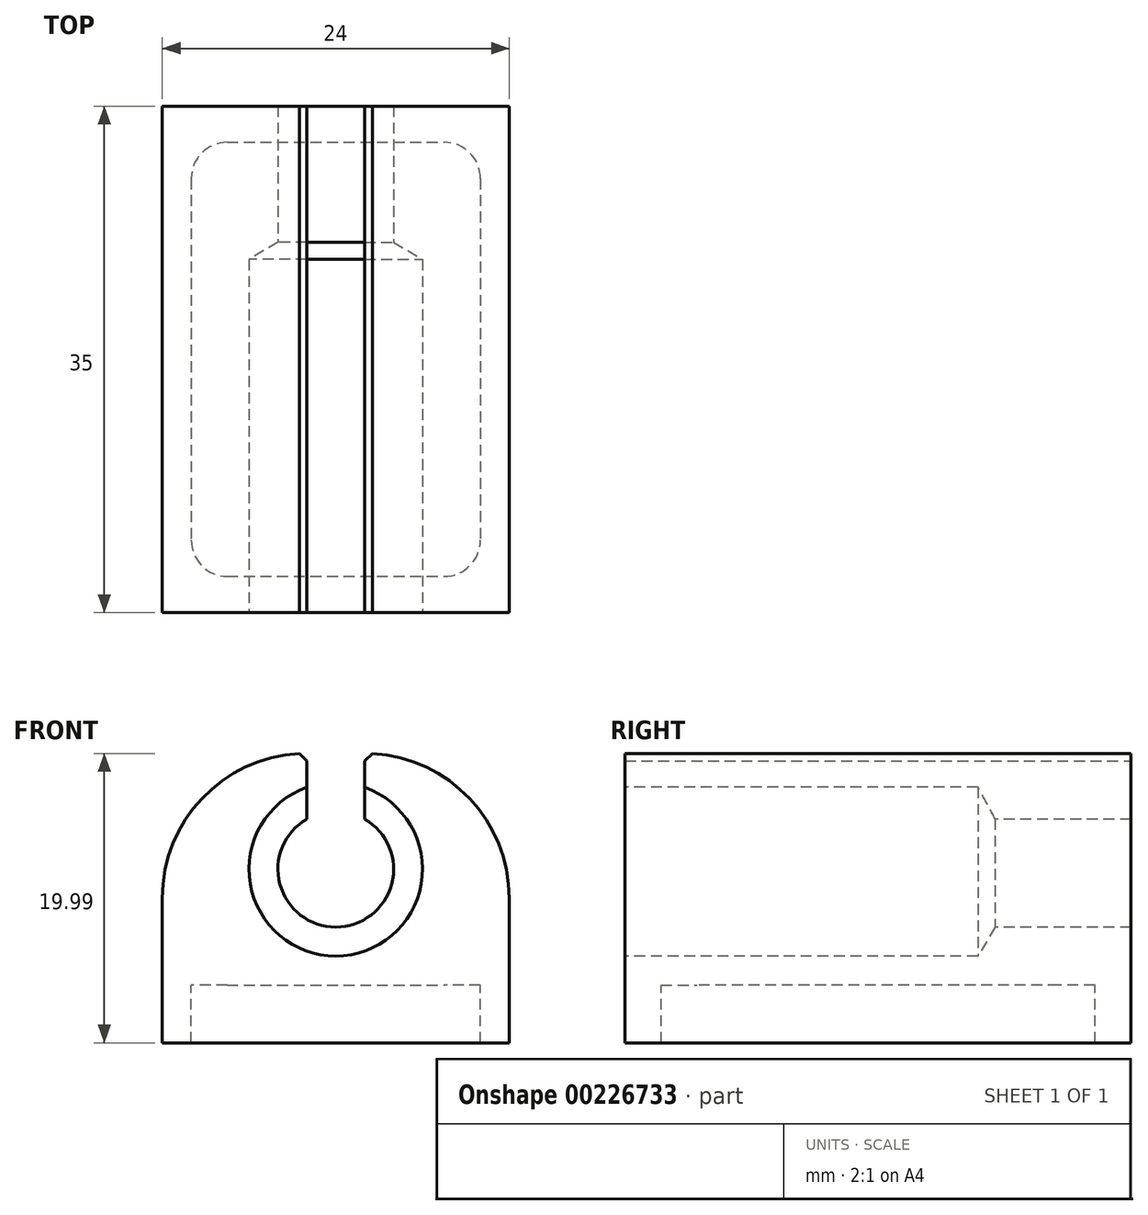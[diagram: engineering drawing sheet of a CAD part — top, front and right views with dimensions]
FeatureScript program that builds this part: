
annotation { "Feature Type Name" : "Feature", "Feature Type Description" : "" }
export const myFeature = defineFeature(function(context is Context, id is Id, definition is map)
    precondition{}
    {
        {
            var Q0;
            Q0=qCreatedBy(makeId("Top.planeOp"),FACE);
            var sketch = newSketch(context, id + "F0", { "sketchPlane" : qUnion([Q0])});
            skLineSegment(sketch, "E0.bottom", {"start": v(0, 12.5) * mm, "end": v(10, 12.5) * mm});
            skLineSegment(sketch, "E0.top", {"start": v(0, -12.5) * mm, "end": v(10, -12.5) * mm});
            skLineSegment(sketch, "E0.left", {"start": v(0, 12.5) * mm, "end": v(0, -12.5) * mm});
            skLineSegment(sketch, "E0.right", {"start": v(10, 12.5) * mm, "end": v(10, -12.5) * mm});
            skLineSegment(sketch, "E1.bottom", {"start": v(0, 12.5) * mm, "end": v(-10, 12.5) * mm});
            skLineSegment(sketch, "E1.top", {"start": v(0, -12.5) * mm, "end": v(-10, -12.5) * mm});
            skLineSegment(sketch, "E1.right", {"start": v(-10, 12.5) * mm, "end": v(-10, -12.5) * mm});
            skLineSegment(sketch, "E2.bottom", {"start": v(-12, 17.5) * mm, "end": v(12, 17.5) * mm});
            skLineSegment(sketch, "E2.top", {"start": v(-12, -17.5) * mm, "end": v(12, -17.5) * mm});
            skLineSegment(sketch, "E2.left", {"start": v(-12, 17.5) * mm, "end": v(-12, -17.5) * mm});
            skLineSegment(sketch, "E2.right", {"start": v(12, 17.5) * mm, "end": v(12, -17.5) * mm});
            skArc(sketch, "E3", {"start": v(-10, 12.5) * mm, "mid": v(-9.27, 14.27) * mm, "end": v(-7.5, 15) * mm});
            skLineSegment(sketch, "E4", {"start": v(-7.5, 15) * mm, "end": v(7.5, 15) * mm});
            skArc(sketch, "E5", {"start": v(10, 12.5) * mm, "mid": v(9.27, 14.27) * mm, "end": v(7.5, 15) * mm});
            skArc(sketch, "E6", {"start": v(10, -12.5) * mm, "mid": v(9.27, -14.27) * mm, "end": v(7.5, -15) * mm});
            skArc(sketch, "E7", {"start": v(-10, -12.5) * mm, "mid": v(-9.27, -14.27) * mm, "end": v(-7.5, -15) * mm});
            skLineSegment(sketch, "E8", {"start": v(-7.5, -15) * mm, "end": v(7.5, -15) * mm});
            skSolve(sketch);
        }
        {
            var Q0;
            Q0=makeQuery(id+"F0.imprint","IMPRINT",FACE,{"disambiguationData":[TD([[makeQuery(id+"F0.imprint","IMPRINT",EDGE,{"derivedFrom":sQuery(id+"F0.wireOp",EDGE,"E0.right")}),1.0]])]});
            extrude(context, id + "F1", {"entities" : qUnion([Q0]), "oppositeDirection" : true, "depth" : 4 * mm});
        }
        {
            var Q0;
            Q0=makeQuery(id+"F0.imprint","IMPRINT",FACE,{"disambiguationData":[TD([[makeQuery(id+"F0.imprint","IMPRINT",EDGE,{"derivedFrom":sQuery(id+"F0.wireOp",EDGE,"E0.bottom")}),-1.0]])]});
            var Q1;
            Q1=makeQuery(id+"F0.imprint","IMPRINT",FACE,{"disambiguationData":[TD([[makeQuery(id+"F0.imprint","IMPRINT",EDGE,{"derivedFrom":sQuery(id+"F0.wireOp",EDGE,"E1.bottom")}),1.0]])]});
            var Q2;
            Q2=makeQuery(id+"F0.imprint","IMPRINT",FACE,{"disambiguationData":[TD([[makeQuery(id+"F0.imprint","IMPRINT",EDGE,{"derivedFrom":sQuery(id+"F0.wireOp",EDGE,"E0.top")}),-1.0]])]});
            var Q3;
            Q3=makeQuery(id+"F0.imprint","IMPRINT",FACE,{"disambiguationData":[TD([[makeQuery(id+"F0.imprint","IMPRINT",EDGE,{"derivedFrom":sQuery(id+"F0.wireOp",EDGE,"E0.bottom")}),1.0]])]});
            var Q4;
            Q4=makeQuery(id+"F0.imprint","IMPRINT",FACE,{"disambiguationData":[TD([[makeQuery(id+"F0.imprint","IMPRINT",EDGE,{"derivedFrom":sQuery(id+"F0.wireOp",EDGE,"E0.right")}),1.0]])]});
            extrude(context, id + "F2", {"entities" : qUnion([Q0, Q1, Q2, Q3, Q4]), "operationType" : NewBodyOperationType.ADD, "depth" : 16 * mm});
        }
        {
            var Q0;
            {var subQ0=sQuery(id+"F0.wireOp",EDGE,"E2.top");Q0=makeQuery(id+"F2.boolean.opBoolean","MERGE",FACE,{"derivedFrom":[makeQuery(id+"F1.opExtrude","SWEPT_FACE",FACE,{"disambiguationData":[OSD([subQ0])]}),makeQuery(id+"F2.opExtrude","SWEPT_FACE",FACE,{"disambiguationData":[OSD([subQ0])]})]});}
            var sketch = newSketch(context, id + "F3", { "sketchPlane" : qUnion([Q0])});
            skPoint(sketch, "E9", {"position": v(0, 8) * mm});
            skPoint(sketch, "E9.positionSnap0", {"position": v(0, -4) * mm});
            skSolve(sketch);
        }
        {
            var Q0;
            Q0=sQuery(id+"F3.wireOp",VERTEX,"E9");
            var Q1;
            Q1=makeQuery(id+"F1.opExtrude","SWEPT_BODY",BODY,{"disambiguationData":[OSD([sQuery(id+"F0.wireOp",EDGE,"E0.right"),sQuery(id+"F0.wireOp",EDGE,"E1.right"),sQuery(id+"F0.wireOp",EDGE,"E2.bottom"),sQuery(id+"F0.wireOp",EDGE,"E2.top"),sQuery(id+"F0.wireOp",EDGE,"E2.left"),sQuery(id+"F0.wireOp",EDGE,"E2.right"),sQuery(id+"F0.wireOp",EDGE,"E3"),sQuery(id+"F0.wireOp",EDGE,"E4"),sQuery(id+"F0.wireOp",EDGE,"E5"),sQuery(id+"F0.wireOp",EDGE,"E6"),sQuery(id+"F0.wireOp",EDGE,"E7"),sQuery(id+"F0.wireOp",EDGE,"E8")])]});
            hole(context, id + "F4", {"style" : HoleStyle.SIMPLE, "endStyle" : HoleEndStyle.BLIND, "standardTappedOrClearance" : lookupTablePath({ "standard" : "ISO", "size" : "12", "type" : "Drilled" }), "standardBlindInLast" : lookupTablePath({ "standard" : "ISO", "size" : "12", "type" : "Drilled" }), "holeDiameter" : 12 * mm, "holeDepth" : (28 - 3.6) * mm, "startFromSketch" : true, "locations" : qUnion([Q0]), "scope" : qUnion([Q1])});
        }
        {
            var Q0;
            Q0=sQuery(id+"F3.wireOp",VERTEX,"E9");
            var Q1;
            Q1=makeQuery(id+"F1.opExtrude","SWEPT_BODY",BODY,{"disambiguationData":[OSD([sQuery(id+"F0.wireOp",EDGE,"E0.right"),sQuery(id+"F0.wireOp",EDGE,"E1.right"),sQuery(id+"F0.wireOp",EDGE,"E2.bottom"),sQuery(id+"F0.wireOp",EDGE,"E2.top"),sQuery(id+"F0.wireOp",EDGE,"E2.left"),sQuery(id+"F0.wireOp",EDGE,"E2.right"),sQuery(id+"F0.wireOp",EDGE,"E3"),sQuery(id+"F0.wireOp",EDGE,"E4"),sQuery(id+"F0.wireOp",EDGE,"E5"),sQuery(id+"F0.wireOp",EDGE,"E6"),sQuery(id+"F0.wireOp",EDGE,"E7"),sQuery(id+"F0.wireOp",EDGE,"E8")])]});
            hole(context, id + "F5", {"style" : HoleStyle.SIMPLE, "endStyle" : HoleEndStyle.THROUGH, "standardTappedOrClearance" : lookupTablePath({ "standard" : "ISO", "size" : "8", "type" : "Drilled" }), "standardBlindInLast" : lookupTablePath({ "standard" : "ISO", "size" : "8", "type" : "Drilled" }), "holeDiameter" : 8 * mm, "startFromSketch" : true, "locations" : qUnion([Q0]), "scope" : qUnion([Q1]), "isTappedThrough" : true});
        }
        {
            var Q0;
            Q0=makeQuery(id+"F2.opExtrude","CAP_FACE",FACE,{"disambiguationData":[OSD([sQuery(id+"F0.wireOp",EDGE,"E2.bottom"),sQuery(id+"F0.wireOp",EDGE,"E2.top"),sQuery(id+"F0.wireOp",EDGE,"E2.left"),sQuery(id+"F0.wireOp",EDGE,"E2.right")])],"isStart":false});
            var sketch = newSketch(context, id + "F6", { "sketchPlane" : qUnion([Q0])});
            skLineSegment(sketch, "E10.bottom", {"start": v(2, 17.5) * mm, "end": v(-2, 17.5) * mm});
            skLineSegment(sketch, "E10.top", {"start": v(2, -17.5) * mm, "end": v(-2, -17.5) * mm});
            skLineSegment(sketch, "E10.left", {"start": v(2, 17.5) * mm, "end": v(2, -17.5) * mm});
            skLineSegment(sketch, "E10.right", {"start": v(-2, 17.5) * mm, "end": v(-2, -17.5) * mm});
            skPoint(sketch, "E10.middle", {"position": v(0, 0) * mm});
            skSolve(sketch);
        }
        {
            var Q0;
            Q0 = qSketchRegion(id + "F6", true);
            extrude(context, id + "F7", {"entities" : qUnion([Q0]), "operationType" : NewBodyOperationType.REMOVE, "endBound" : BoundingType.UP_TO_NEXT, "oppositeDirection" : true, "depth" : 25 * mm});
        }
        {
            var Q0;
            Q0=makeQuery(id+"F2.opExtrude","CAP_EDGE",EDGE,{"disambiguationData":[OSD([sQuery(id+"F0.wireOp",EDGE,"E2.right")])],"isStart":false});
            var Q1;
            Q1=makeQuery(id+"F2.opExtrude","CAP_EDGE",EDGE,{"disambiguationData":[OSD([sQuery(id+"F0.wireOp",EDGE,"E2.left")])],"isStart":false});
            fillet(context, id + "F8", {"entities" : qUnion([Q0, Q1]), "radius" : 10 * mm, "tangentPropagation" : true, "allowEdgeOverflow" : false});
        }
        {
            var Q0;
            Q0=makeQuery(id+"F8.opFillet","BLEND_EDGE",EDGE,{"blendedFrom":[makeQuery(id+"F2.opExtrude","CAP_EDGE",EDGE,{"disambiguationData":[OSD([sQuery(id+"F0.wireOp",EDGE,"E2.left")])],"isStart":false}),makeQuery(id+"F7.boolean.opBoolean","COPY",FACE,{"derivedFrom":makeQuery(id+"F7.opExtrude","SWEPT_FACE",FACE,{"disambiguationData":[OSD([sQuery(id+"F6.wireOp",EDGE,"E10.right")])]})})],"blendedInto":[makeQuery(id+"F7.boolean.opBoolean","COPY",FACE,{"derivedFrom":makeQuery(id+"F7.opExtrude","SWEPT_FACE",FACE,{"disambiguationData":[OSD([sQuery(id+"F6.wireOp",EDGE,"E10.right")])]})})]});
            var Q1;
            Q1=makeQuery(id+"F8.opFillet","BLEND_EDGE",EDGE,{"blendedFrom":[makeQuery(id+"F2.opExtrude","CAP_EDGE",EDGE,{"disambiguationData":[OSD([sQuery(id+"F0.wireOp",EDGE,"E2.right")])],"isStart":false}),makeQuery(id+"F7.boolean.opBoolean","COPY",FACE,{"derivedFrom":makeQuery(id+"F7.opExtrude","SWEPT_FACE",FACE,{"disambiguationData":[OSD([sQuery(id+"F6.wireOp",EDGE,"E10.left")])]})})],"blendedInto":[makeQuery(id+"F7.boolean.opBoolean","COPY",FACE,{"derivedFrom":makeQuery(id+"F7.opExtrude","SWEPT_FACE",FACE,{"disambiguationData":[OSD([sQuery(id+"F6.wireOp",EDGE,"E10.left")])]})})]});
            var Q2;
            Q2=makeQuery(id+"F7.boolean.opBoolean","COPY",EDGE,{"derivedFrom":makeQuery(id+"F7.opExtrude","SWEPT_EDGE",EDGE,{"disambiguationData":[OSD([sQuery(id+"F0.wireOp",EDGE,"E2.top"),sQuery(id+"F6.wireOp",EDGE,"E10.top"),sQuery(id+"F6.wireOp",EDGE,"E10.right")])]})});
            var Q3;
            Q3=makeQuery(id+"F7.boolean.opBoolean","COPY",EDGE,{"derivedFrom":makeQuery(id+"F7.opExtrude","SWEPT_EDGE",EDGE,{"disambiguationData":[OSD([sQuery(id+"F0.wireOp",EDGE,"E2.top"),sQuery(id+"F6.wireOp",EDGE,"E10.top"),sQuery(id+"F6.wireOp",EDGE,"E10.left")])]})});
            var Q4;
            Q4=makeQuery(id+"F4.hole-0.boolean.opBoolean","COPY",EDGE,{"derivedFrom":makeQuery(id+"F4.hole-0.opRevolve","SWEPT_EDGE",EDGE,{"disambiguationData":[OSD([sQuery(id+"F4.hole-0.sketch.wireOp",EDGE,"core_line_2"),sQuery(id+"F4.hole-0.sketch.wireOp",EDGE,"core_line_3")])]})});
            var Q5;
            Q5=makeQuery(id+"F7.boolean.opBoolean","COPY",EDGE,{"derivedFrom":makeQuery(id+"F7.opExtrude","SWEPT_EDGE",EDGE,{"disambiguationData":[OSD([sQuery(id+"F0.wireOp",EDGE,"E2.bottom"),sQuery(id+"F6.wireOp",EDGE,"E10.bottom"),sQuery(id+"F6.wireOp",EDGE,"E10.left")])]})});
            var Q6;
            Q6=makeQuery(id+"F7.boolean.opBoolean","COPY",EDGE,{"derivedFrom":makeQuery(id+"F7.opExtrude","SWEPT_EDGE",EDGE,{"disambiguationData":[OSD([sQuery(id+"F0.wireOp",EDGE,"E2.bottom"),sQuery(id+"F6.wireOp",EDGE,"E10.bottom"),sQuery(id+"F6.wireOp",EDGE,"E10.right")])]})});
            var Q7;
            {var subQ0=sQuery(id+"F0.wireOp",EDGE,"E2.bottom");Q7=makeQuery(id+"F5.hole-0.boolean.opBoolean","INTERSECT",EDGE,{"derivedFrom":[makeQuery(id+"F2.boolean.opBoolean","MERGE",FACE,{"derivedFrom":[makeQuery(id+"F1.opExtrude","SWEPT_FACE",FACE,{"disambiguationData":[OSD([subQ0])]}),makeQuery(id+"F2.opExtrude","SWEPT_FACE",FACE,{"disambiguationData":[OSD([subQ0])]})]}),makeQuery(id+"F5.hole-0.opRevolve","SWEPT_FACE",FACE,{"disambiguationData":[OSD([sQuery(id+"F5.hole-0.sketch.wireOp",EDGE,"core_line_2")])]})]});}
            chamfer(context, id + "F9", {"entities" : qUnion([Q0, Q1, Q2, Q3, Q4, Q5, Q6, Q7]), "width" : 0.5 * mm, "tangentPropagation" : true});
        }
    });
